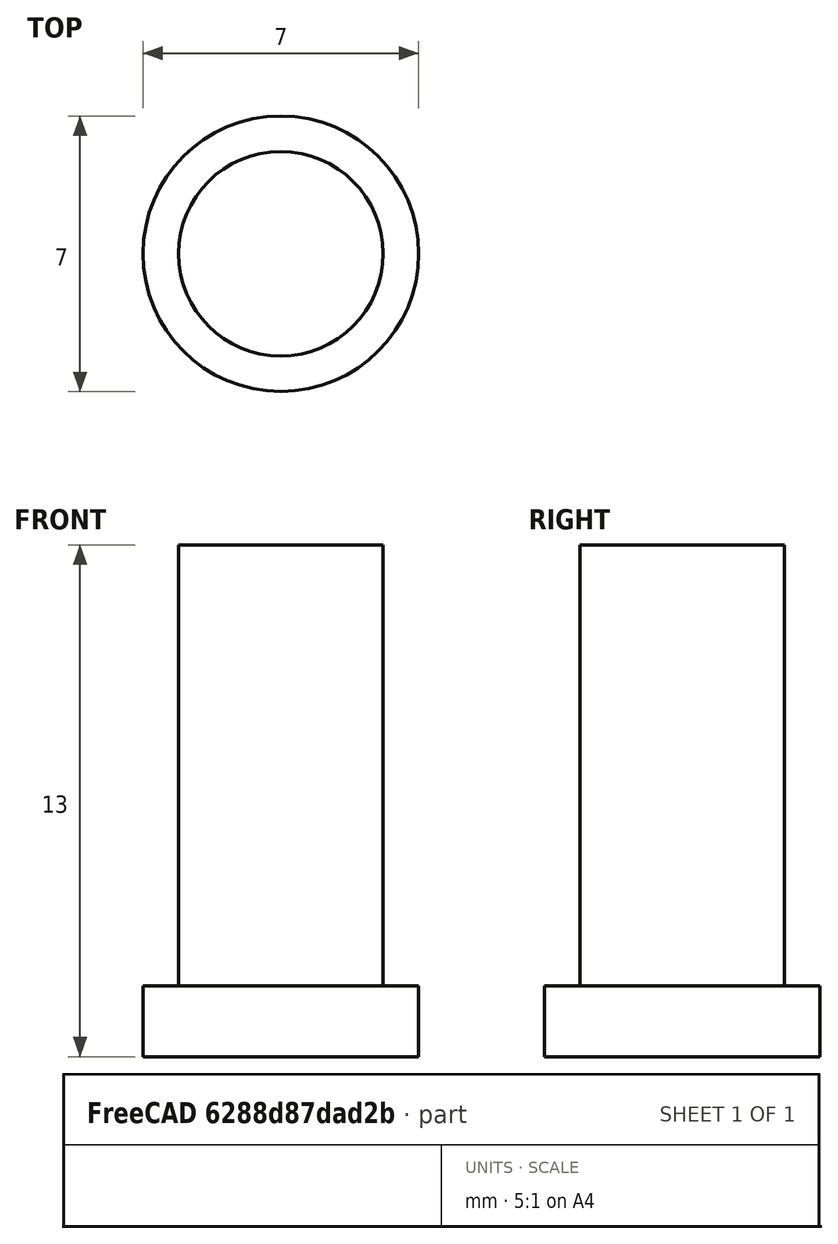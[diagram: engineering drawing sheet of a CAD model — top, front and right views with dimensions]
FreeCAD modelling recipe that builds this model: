
FCSTD DOCUMENT  (FreeCAD 0.16R6706 (Git))
Label: ButtonBig
License: All rights reserved
LicenseURL: http://de.wikipedia.org/wiki/Alle_Rechte_vorbehalten
objects: Sketcher::SketchObject×1, PartDesign::Revolution×1
note: 3 computed .brp shape members not serialized (recipe doc carries the construction recipe); baked Part::Feature solids carry a one-line shape summary decoded from their .brp

FEATURE [Sketcher::SketchObject] Sketch
  Placement = pos=(0,0,0) rot=(1,0,0;1.5708rad)
  sketch-geometry (6):
    g0: LineSegment StartX=0 StartY=13 StartZ=0 EndX=2.6 EndY=13 EndZ=0
    g1: LineSegment StartX=2.6 StartY=13 StartZ=0 EndX=2.6 EndY=1.8 EndZ=0
    g2: LineSegment StartX=2.6 StartY=1.8 StartZ=0 EndX=3.5 EndY=1.8 EndZ=0
    g3: LineSegment StartX=3.5 StartY=1.8 StartZ=0 EndX=3.5 EndY=0 EndZ=0
    g4: LineSegment StartX=3.5 StartY=0 StartZ=0 EndX=0 EndY=0 EndZ=0
    g5: LineSegment StartX=0 StartY=0 StartZ=0 EndX=0 EndY=13 EndZ=0
  constraints (17):
    c: PointOnObject(g0,g-2)
    c: Horizontal(g0)
    c: Coincident(g1,g0)
    c: Vertical(g1)
    c: Coincident(g2,g1)
    c: Horizontal(g2)
    c: Coincident(g3,g2)
    c: PointOnObject(g3,g-1)
    c: Coincident(g4,g3)
    c: Coincident(g4,g-1)
    c: Coincident(g5,g-1)
    c: Coincident(g5,g0)
    c: Vertical(g3)
    c: DistanceX(g0,g0) = 2.6
    c: DistanceX(g-1,g3) = 3.5
    c: DistanceY(g-1,g0) = 13
    c: DistanceY(g3,g2) = 1.8
FEATURE [PartDesign::Revolution] Revolution
  Angle = 360
  Axis = (0,0,1)
  Base = (0,0,0)
  Placement = pos=(0,0,0) rot=(1,0,0;1.5708rad)
  ReferenceAxis = -> Sketch [V_Axis]
  Reversed = true
  Sketch = -> Sketch
